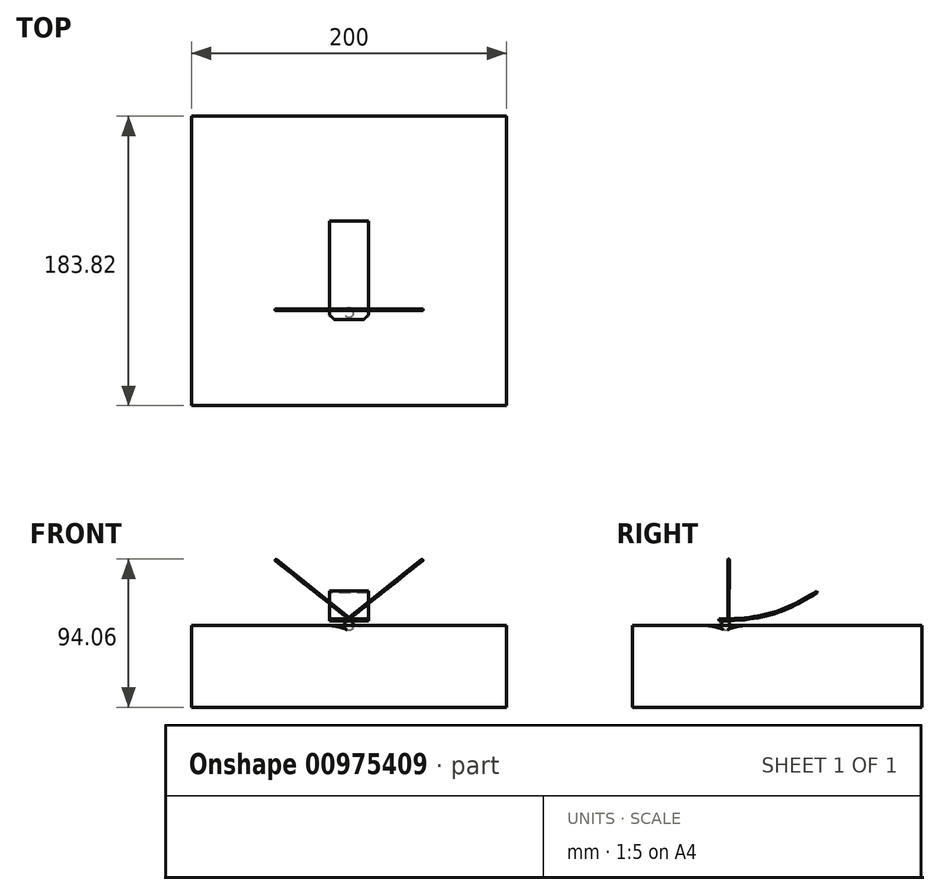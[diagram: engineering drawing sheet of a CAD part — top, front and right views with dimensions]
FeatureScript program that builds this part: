
annotation { "Feature Type Name" : "Feature", "Feature Type Description" : "" }
export const myFeature = defineFeature(function(context is Context, id is Id, definition is map)
    precondition{}
    {
        {
            var Q0;
            Q0=qCreatedBy(makeId("Right.planeOp"),FACE);
            var sketch = newSketch(context, id + "F0", { "sketchPlane" : qUnion([Q0])});
            skArc(sketch, "E0", {"start": v(-32.81, -6) * mm, "mid": v(-29.81, -3) * mm, "end": v(-32.81, 0) * mm});
            skLineSegment(sketch, "E1", {"start": v(-32.81, 0) * mm, "end": v(-32.81, -6) * mm});
            skSolve(sketch);
        }
        {
            var Q0;
            Q0=makeQuery(id+"F0.imprint","IMPRINT",FACE,{"disambiguationData":[TD([[makeQuery(id+"F0.imprint","IMPRINT",EDGE,{"derivedFrom":sQuery(id+"F0.wireOp",EDGE,"E0")}),1.0]])]});
            var Q1;
            Q1=sQuery(id+"F0.wireOp",EDGE,"E1");
            revolve(context, id + "F1", {"surfaceOperationType" : NewSurfaceOperationType.NEW, "entities" : qUnion([Q0]), "axis" : qUnion([Q1]), "revolveType" : RevolveType.FULL});
        }
        {
            var Q0;
            Q0=qCreatedBy(makeId("Top.planeOp"),FACE);
            var sketch = newSketch(context, id + "F2", { "sketchPlane" : qUnion([Q0])});
            skLineSegment(sketch, "E2.bottom", {"start": v(100, 91.91) * mm, "end": v(-100, 91.91) * mm});
            skLineSegment(sketch, "E2.top", {"start": v(100, -91.91) * mm, "end": v(-100, -91.91) * mm});
            skLineSegment(sketch, "E2.left", {"start": v(100, 91.91) * mm, "end": v(100, -91.91) * mm});
            skLineSegment(sketch, "E2.right", {"start": v(-100, 91.91) * mm, "end": v(-100, -91.91) * mm});
            skPoint(sketch, "E2.middle", {"position": v(0, 0) * mm});
            skSolve(sketch);
        }
        {
            var Q0;
            Q0 = qSketchRegion(id + "F2", true);
            extrude(context, id + "F3", {"entities" : qUnion([Q0]), "oppositeDirection" : true, "depth" : 55 * mm, "offsetDistance" : 25 * mm, "hasSecondDirection" : true, "secondDirectionOppositeDirection" : true, "secondDirectionDepth" : 3 * mm});
        }
        {
            var Q0;
            Q0=makeQuery(id+"F1.opRevolve","SWEPT_BODY",BODY,{"disambiguationData":[OSD([sQuery(id+"F0.wireOp",EDGE,"E0"),sQuery(id+"F0.wireOp",EDGE,"E1")])]});
            var Q1;
            Q1=makeQuery(id+"F3.opExtrude","SWEPT_BODY",BODY,{"disambiguationData":[OSD([sQuery(id+"F2.wireOp",EDGE,"E2.bottom"),sQuery(id+"F2.wireOp",EDGE,"E2.top"),sQuery(id+"F2.wireOp",EDGE,"E2.left"),sQuery(id+"F2.wireOp",EDGE,"E2.right")])]});
            booleanBodies(context, id + "F4", {"operationType" : BooleanOperationType.SUBTRACTION, "tools" : qUnion([Q0]), "targets" : qUnion([Q1]), "keepTools" : true});
        }
        {
            var Q0;
            Q0=makeQuery(id+"F4.opBoolean","INTERSECT",EDGE,{"derivedFrom":[makeQuery(id+"F1.opRevolve","SWEPT_FACE",FACE,{"disambiguationData":[OSD([sQuery(id+"F0.wireOp",EDGE,"E0")])]}),makeQuery(id+"F3.opExtrude","CAP_FACE",FACE,{"disambiguationData":[OSD([sQuery(id+"F2.wireOp",EDGE,"E2.bottom"),sQuery(id+"F2.wireOp",EDGE,"E2.top"),sQuery(id+"F2.wireOp",EDGE,"E2.left"),sQuery(id+"F2.wireOp",EDGE,"E2.right")])],"isStart":true})]});
            fillet(context, id + "F5", {"entities" : qUnion([Q0]), "radius" : 31.15 * mm, "tangentPropagation" : true, "allowEdgeOverflow" : false});
        }
        {
            var Q0;
            Q0=qCreatedBy(makeId("Right.planeOp"),FACE);
            var sketch = newSketch(context, id + "F6", { "sketchPlane" : qUnion([Q0])});
            skFitSpline(sketch, "E3", {"points": [v(-37.1, -0.24) * mm, v(25.2, 17.57) * mm], "startDerivative": vector(90.46, 0.73) * mm, "endDerivative": vector(55.81, 35.02) * mm});
            skLineSegment(sketch, "E4", {"start": v(-37.1, -0.24) * mm, "end": v(-37.1, 0.94) * mm});
            skLineSegment(sketch, "E5", {"start": v(25.2, 17.57) * mm, "end": v(25.2, 18.76) * mm});
            skFitSpline(sketch, "E6", {"points": [v(-37.1, 0.94) * mm, v(25.2, 18.76) * mm], "startDerivative": vector(90.46, 0.73) * mm, "endDerivative": vector(55.81, 35.02) * mm});
            skSolve(sketch);
        }
        {
            var Q0;
            Q0 = qSketchRegion(id + "F6", true);
            extrude(context, id + "F7", {"entities" : qUnion([Q0]), "depth" : 25 * mm, "offsetDistance" : 25 * mm, "symmetric" : true});
        }
        {
            var Q0;
            Q0=qCreatedBy(makeId("Front.planeOp"),FACE);
            cPlane(context, id + "F8", {"entities" : qUnion([Q0]), "cplaneType" : CPlaneType.OFFSET, "offset" : 30.9 * mm, "width" : 150 * mm, "height" : 150 * mm});
        }
        {
            var Q0;
            Q0=qCreatedBy(id+"F8.planeOp",FACE);
            var sketch = newSketch(context, id + "F9", { "sketchPlane" : qUnion([Q0])});
            skLineSegment(sketch, "E7", {"start": v(0.1, 0.96) * mm, "end": v(47.08, 38.27) * mm});
            skLineSegment(sketch, "E8", {"start": v(47.08, 38.27) * mm, "end": v(46.77, 38.66) * mm});
            skLineSegment(sketch, "E9", {"start": v(46.77, 38.66) * mm, "end": v(0.03, 1.45) * mm});
            skLineSegment(sketch, "E10", {"start": v(0.03, 1.45) * mm, "end": v(0.1, 0.96) * mm});
            skSolve(sketch);
        }
        {
            var Q0;
            Q0=makeQuery(id+"F9.imprint","IMPRINT",FACE,{"disambiguationData":[TD([[makeQuery(id+"F9.imprint","IMPRINT",EDGE,{"derivedFrom":sQuery(id+"F9.wireOp",EDGE,"E7")}),1.0]])]});
            var Q1;
            Q1=sQuery(id+"F9.wireOp",EDGE,"E7");
            var Q2;
            Q2=sQuery(id+"F9.wireOp",EDGE,"E9");
            revolve(context, id + "F10", {"surfaceOperationType" : NewSurfaceOperationType.NEW, "entities" : qUnion([Q0]), "surfaceEntities" : qUnion([Q1]), "axis" : qUnion([Q2]), "revolveType" : RevolveType.FULL});
        }
        {
            var Q0;
            Q0=makeQuery(id+"F7.opExtrude","SWEPT_BODY",BODY,{"disambiguationData":[OSD([sQuery(id+"F6.wireOp",EDGE,"E3"),sQuery(id+"F6.wireOp",EDGE,"E4"),sQuery(id+"F6.wireOp",EDGE,"E5"),sQuery(id+"F6.wireOp",EDGE,"E6")])]});
            var Q1;
            Q1=makeQuery(id+"F10.opRevolve","SWEPT_BODY",BODY,{"disambiguationData":[OSD([sQuery(id+"F9.wireOp",EDGE,"E7"),sQuery(id+"F9.wireOp",EDGE,"E8"),sQuery(id+"F9.wireOp",EDGE,"E9"),sQuery(id+"F9.wireOp",EDGE,"E10")])]});
            booleanBodies(context, id + "F11", {"operationType" : BooleanOperationType.SUBTRACTION, "tools" : qUnion([Q0]), "targets" : qUnion([Q1]), "keepTools" : true});
        }
        {
            var Q0;
            Q0=makeQuery(id+"F10.opRevolve","SWEPT_BODY",BODY,{"disambiguationData":[OSD([sQuery(id+"F9.wireOp",EDGE,"E7")])]});
            var Q1;
            Q1=qCreatedBy(makeId("Right.planeOp"),FACE);
            mirror(context, id + "F12", {"entities" : qUnion([Q0]), "mirrorPlane" : qUnion([Q1])});
        }
        {
            var Q0;
            Q0=makeQuery(id+"F7.opExtrude","CAP_EDGE",EDGE,{"disambiguationData":[OSD([sQuery(id+"F6.wireOp",EDGE,"E4")])],"isStart":false});
            var Q1;
            Q1=makeQuery(id+"F7.opExtrude","CAP_EDGE",EDGE,{"disambiguationData":[OSD([sQuery(id+"F6.wireOp",EDGE,"E4")])],"isStart":true});
            chamfer(context, id + "F13", {"entities" : qUnion([Q0, Q1]), "width" : 3 * mm, "tangentPropagation" : true});
        }
    });
